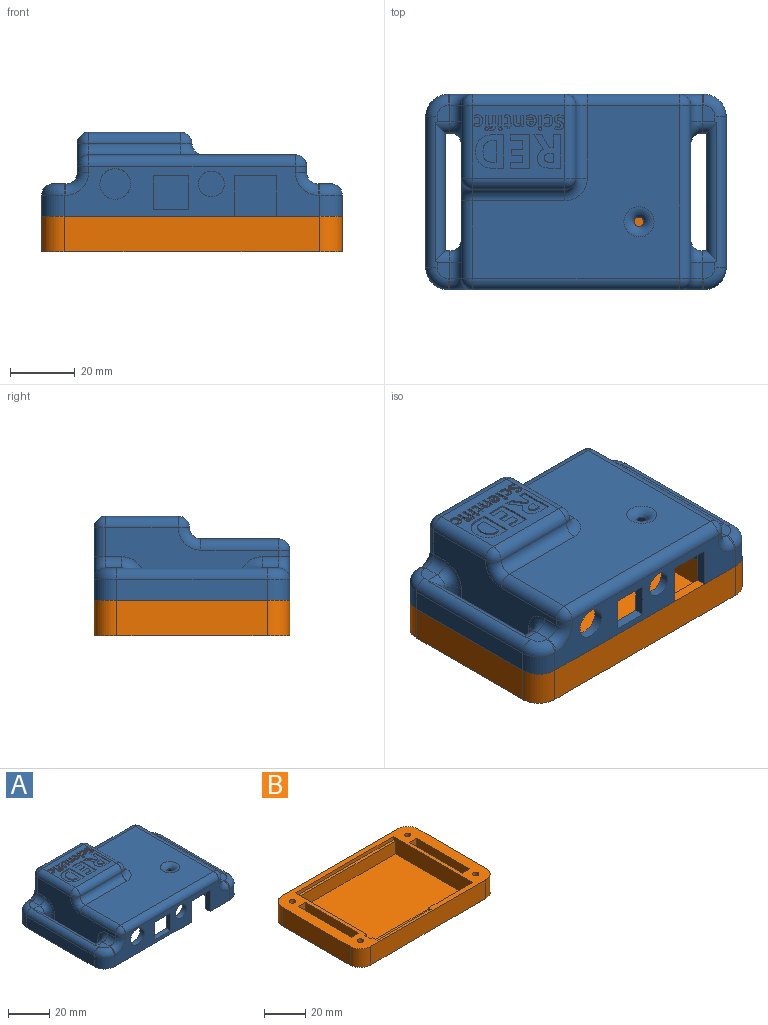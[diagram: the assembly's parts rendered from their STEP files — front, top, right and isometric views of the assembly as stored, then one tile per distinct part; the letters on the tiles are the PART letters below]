
ASSEMBLY  parts=2 mates=1
PART A: 327 faces, bbox 94.2x61.7x26 mm
  f0: plane 28.5x22.5mm, normal (0,0,1), area 406.2mm2, adj f59,f61,f65,f67,f109,f110,f111,f112
  f1: plane 5x4mm, normal (0,0,1), area 17.4mm2, adj f56,f57,f62,f69,f70
  f2: plane 5x4mm, normal (0,0,1), area 17.4mm2, adj f74,f76,f82,f83,f90
  f3: plane 79x15.5mm, normal (0,-1,0), area 711.4mm2, adj f5,f11,f19,f29,f30,f31,f32,f33
  f4: plane 67x17mm, normal (0,1,0), area 739.9mm2, adj f5,f25,f26,f27,f29,f30,f31,f32
  f5: plane 93x60.5mm, normal (0,0,-1), area 1410.7mm2, adj f3,f4,f6,f7,f8,f10,f11,f12
  f6: plane 53.5x22.5mm, normal (-1,0,0), area 694.3mm2, adj f5,f46,f47,f50,f51,f58,f59,f63
  f7: plane 53.5x15.5mm, normal (1,0,0), area 526.3mm2, adj f5,f73,f74,f75,f87,f88,f93,f96
  f8: plane 79x22.5mm, normal (0,1,0), area 1320.5mm2, adj f5,f13,f17,f48,f49,f51,f61,f76
  f9: plane 64x53.5mm, normal (0,0,1), area 2319mm2, adj f66,f71,f72,f85,f86,f95,f96,f108
  f10: plane 6.5x1.5mm, normal (0,1,0), area 9.8mm2, adj f5,f15,f88,f89
  f11: cylinder r=7mm len=7mm, axis (0,0,-1), area 71.5mm2, adj f3,f5,f12,f94
  f12: plane 46.5x6.5mm, normal (1,0,0), area 302.2mm2, adj f5,f11,f13,f90
  f13: cylinder r=7mm len=7mm, axis (0,0,-1), area 71.5mm2, adj f5,f8,f12,f83
  f14: plane 6.5x1.5mm, normal (0,-1,0), area 9.8mm2, adj f5,f15,f73,f82
  f15: plane 36.5x6.5mm, normal (-1,0,0), area 237.2mm2, adj f5,f10,f14,f81
  f16: plane 5x4mm, normal (0,0,1), area 17.4mm2, adj f89,f90,f94,f97,f98
  f17: cylinder r=7mm len=7mm, axis (0,0,-1), area 71.5mm2, adj f5,f8,f18,f52
  f18: plane 46.5x6.5mm, normal (-1,0,0), area 302.2mm2, adj f5,f17,f19,f56
  f19: cylinder r=7mm len=7mm, axis (0,0,-1), area 71.5mm2, adj f3,f5,f18,f62
  f20: plane 6.5x1.5mm, normal (0,1,0), area 9.8mm2, adj f5,f21,f57,f58
  f21: plane 36.5x6.5mm, normal (1,0,0), area 237.3mm2, adj f5,f20,f22,f54
  f22: plane 6.5x1.5mm, normal (0,-1,0), area 9.8mm2, adj f5,f21,f47,f53
  f23: plane 5x4mm, normal (0,0,1), area 17.4mm2, adj f46,f49,f52,f53,f56
  f24: plane 67x20.5mm, normal (0,-1,0), area 1251.9mm2, adj f5,f25,f26,f27,f102,f106
  f25: plane 56x20.5mm, normal (1,0,0), area 1045.6mm2, adj f4,f5,f24,f27,f103,f107
  f26: plane 56x17mm, normal (-1,0,0), area 952mm2, adj f4,f5,f24,f27
  f27: plane 67x56mm, normal (0,0,-1), area 2712.4mm2, adj f4,f24,f25,f26,f102,f103,f108
  f28: plane 24.5x19mm, normal (0,0,-1), area 465.5mm2, adj f104,f105,f106,f107
  f29: plane 11x3mm, normal (0,0,-1), area 33mm2, adj f3,f4,f30,f32
  f30: plane 10.5x3mm, normal (1,0,0), area 31.5mm2, adj f3,f4,f29,f31
  f31: plane 11x3mm, normal (0,0,1), area 33mm2, adj f3,f4,f30,f32
  f32: plane 10.5x3mm, normal (-1,0,0), area 31.5mm2, adj f3,f4,f29,f31
  f33: plane 12.5x3mm, normal (-1,0,0), area 37.5mm2, adj f3,f4,f5,f34
  f34: plane 13x3mm, normal (0,0,-1), area 39mm2, adj f3,f4,f33,f35
  f35: plane 12.5x3mm, normal (1,0,0), area 37.5mm2, adj f3,f4,f5,f34
  f36: cylinder r=4mm len=8mm, axis (0,-1,0), area 75.4mm2, adj f3,f4
  f37: cylinder r=4.75mm len=9.5mm, axis (0,-1,0), area 89.5mm2, adj f3,f4
  f38: cone r=0mm half-angle=59deg, axis (0,0,-1), area 8.2mm2, adj f39
  f39: cylinder r=1.5mm len=5mm, axis (0,0,-1), area 47.1mm2, adj f5,f38
  f40: cone r=0mm half-angle=59deg, axis (0,0,-1), area 8.2mm2, adj f41
  f41: cylinder r=1.5mm len=5mm, axis (0,0,-1), area 47.1mm2, adj f5,f40
  f42: cone r=0mm half-angle=59deg, axis (0,0,-1), area 8.2mm2, adj f43
  f43: cylinder r=1.5mm len=5mm, axis (0,0,-1), area 47.1mm2, adj f5,f42
  f44: cone r=0mm half-angle=59deg, axis (0,0,-1), area 8.2mm2, adj f45
  f45: cylinder r=1.5mm len=5mm, axis (0,0,-1), area 47.1mm2, adj f5,f44
  f46: cylinder r=3.5mm len=5mm, axis (0,1,0), area 27.5mm2, adj f6,f23,f48,f50
  f47: cylinder r=3.5mm len=6.5mm, axis (0,0,-1), area 35.7mm2, adj f5,f6,f22,f50
  f48: torus R=7mm, axis (0,1,0), area 41.2mm2, adj f8,f46,f49,f51
  f49: cylinder r=3.5mm len=3.5mm, axis (-1,0,0), area 2.7mm2, adj f8,f23,f48,f52
  f50: torus R=7mm, axis (1,0,0), area 41.2mm2, adj f6,f46,f47,f53
  f51: cylinder r=3.5mm len=9mm, axis (0,0,1), area 49.5mm2, adj f6,f8,f48,f55
  f52: torus R=3.5mm, axis (0,0,1), area 49.5mm2, adj f17,f23,f49,f56
  f53: cylinder r=3.5mm len=4.5mm, axis (-1,0,0), area 15mm2, adj f22,f23,f50,f54,f56
  f54: cylinder r=3.5mm len=42.5mm, axis (0,-1,0), area 193.1mm2, adj f21,f53,f56,f57
  f55: sphere r=3.5mm, area 19.2mm2, adj f51,f59,f61
  f56: cylinder r=3.5mm len=46.5mm, axis (0,1,0), area 234.1mm2, adj f1,f18,f23,f52,f53,f54,f57,f62
  f57: cylinder r=3.5mm len=4.5mm, axis (1,0,0), area 15mm2, adj f1,f20,f54,f56,f63
  f58: cylinder r=3.5mm len=6.5mm, axis (0,0,1), area 35.7mm2, adj f5,f6,f20,f63
  f59: cylinder r=3.5mm len=22.5mm, axis (0,-1,0), area 123.7mm2, adj f0,f6,f55,f64
  f60: sphere r=3.5mm, area 19.2mm2, adj f65,f66,f67
  f61: cylinder r=3.5mm len=28.5mm, axis (1,0,0), area 156.7mm2, adj f0,f8,f55,f68
  f62: torus R=3.5mm, axis (0,0,1), area 49.5mm2, adj f1,f19,f56,f69
  f63: torus R=7mm, axis (1,0,0), area 41.2mm2, adj f6,f57,f58,f70
  f64: sphere r=3.5mm, area 19.2mm2, adj f59,f65,f78
  f65: cylinder r=3.5mm len=28.5mm, axis (-1,0,0), area 156.7mm2, adj f0,f60,f64,f71
  f66: torus R=7mm, axis (0,0,1), area 41.2mm2, adj f9,f60,f71,f72
  f67: cylinder r=3.5mm len=22.5mm, axis (0,-1,0), area 123.7mm2, adj f0,f60,f68,f72
  f68: sphere r=3.5mm, area 19.2mm2, adj f61,f67,f79
  f69: cylinder r=3.5mm len=3.5mm, axis (-1,0,0), area 2.7mm2, adj f1,f3,f62,f77
  f70: cylinder r=3.5mm len=5mm, axis (0,-1,0), area 27.5mm2, adj f1,f6,f63,f77
  f71: cylinder r=3.5mm len=28.5mm, axis (1,0,0), area 156.7mm2, adj f9,f65,f66,f78
  f72: cylinder r=3.5mm len=22.5mm, axis (0,1,0), area 123.7mm2, adj f9,f66,f67,f79
  f73: cylinder r=3.5mm len=6.5mm, axis (0,0,-1), area 35.7mm2, adj f5,f7,f14,f75
  f74: cylinder r=3.5mm len=5mm, axis (0,-1,0), area 27.5mm2, adj f2,f7,f75,f80
  f75: torus R=7mm, axis (1,0,0), area 41.2mm2, adj f7,f73,f74,f82
  f76: cylinder r=3.5mm len=3.5mm, axis (1,0,0), area 2.7mm2, adj f2,f8,f80,f83
  f77: torus R=7mm, axis (0,1,0), area 41.2mm2, adj f3,f69,f70,f84
  f78: torus R=7mm, axis (1,0,0), area 41.2mm2, adj f6,f64,f71,f85
  f79: torus R=7mm, axis (0,1,0), area 41.2mm2, adj f8,f68,f72,f86
  f80: torus R=7mm, axis (0,1,0), area 41.2mm2, adj f8,f74,f76,f87
  f81: cylinder r=3.5mm len=42.5mm, axis (0,1,0), area 193.1mm2, adj f15,f82,f89,f90
  f82: cylinder r=3.5mm len=4.5mm, axis (-1,0,0), area 15mm2, adj f2,f14,f75,f81,f90
  f83: torus R=3.5mm, axis (0,0,1), area 49.5mm2, adj f2,f13,f76,f90
  f84: cylinder r=3.5mm len=3.5mm, axis (0,0,-1), area 11mm2, adj f3,f6,f77,f91
  f85: cylinder r=3.5mm len=24mm, axis (0,1,0), area 131.9mm2, adj f6,f9,f78,f91
  f86: cylinder r=3.5mm len=28.5mm, axis (1,0,0), area 156.7mm2, adj f8,f9,f79,f92
  f87: cylinder r=3.5mm len=3.5mm, axis (0,0,-1), area 11mm2, adj f7,f8,f80,f92
  f88: cylinder r=3.5mm len=6.5mm, axis (0,0,1), area 35.7mm2, adj f5,f7,f10,f93
  f89: cylinder r=3.5mm len=4.5mm, axis (1,0,0), area 15mm2, adj f10,f16,f81,f90,f93
  f90: cylinder r=3.5mm len=46.5mm, axis (0,-1,0), area 234.1mm2, adj f2,f12,f16,f81,f82,f83,f89,f94
  f91: sphere r=3.5mm, area 19.2mm2, adj f84,f85,f95
  f92: sphere r=3.5mm, area 19.2mm2, adj f86,f87,f96
  f93: torus R=7mm, axis (1,0,0), area 41.2mm2, adj f7,f88,f89,f97
  f94: torus R=3.5mm, axis (0,0,1), area 49.5mm2, adj f11,f16,f90,f98
  f95: cylinder r=3.5mm len=64mm, axis (-1,0,0), area 351.9mm2, adj f3,f9,f91,f99
  f96: cylinder r=3.5mm len=53.5mm, axis (0,-1,0), area 294.1mm2, adj f7,f9,f92,f99
  f97: cylinder r=3.5mm len=5mm, axis (0,1,0), area 27.5mm2, adj f7,f16,f93,f100
  f98: cylinder r=3.5mm len=3.5mm, axis (1,0,0), area 2.7mm2, adj f3,f16,f94,f100
  f99: sphere r=3.5mm, area 19.2mm2, adj f95,f96,f101
  f100: torus R=7mm, axis (0,1,0), area 41.2mm2, adj f3,f97,f98,f101
  f101: cylinder r=3.5mm len=3.5mm, axis (0,0,1), area 11mm2, adj f3,f7,f99,f100
  f102: cylinder r=3.5mm len=29.5mm, axis (0,-1,0), area 149.9mm2, adj f24,f27,f103,f104
  f103: cylinder r=3.5mm len=35mm, axis (-1,0,0), area 180.2mm2, adj f25,f27,f102,f105
  f104: cylinder r=3.5mm len=26mm, axis (0,1,0), area 129mm2, adj f28,f102,f105,f106
  f105: cylinder r=3.5mm len=31.5mm, axis (1,0,0), area 159.2mm2, adj f28,f103,f104,f107
  f106: cylinder r=3.5mm len=31.5mm, axis (-1,0,0), area 159.2mm2, adj f24,f28,f104,f107
  f107: cylinder r=3.5mm len=26mm, axis (0,-1,0), area 129mm2, adj f25,f28,f105,f106
  f108: torus R=4.66mm, axis (0,0,1), area 71.7mm2, adj f9,f27
  f109: plane 3.97x0.5mm, normal (1,0,0), area 2mm2, adj f0,f110,f127,f128
  f110: plane 1.17x0.5mm, normal (0,-1,0), area 0.6mm2, adj f0,f109,f111,f128
  f111: plane 3.97x2.47mm, normal (-0.85,-0.53,0), area 2.3mm2, adj f0,f110,f112,f128
  f112: plane 2.43x0.5mm, normal (0,-1,0), area 1.2mm2, adj f0,f111,f113,f128
  f113: extruded ~4.51x3.04mm, area 2.7mm2, adj f0,f112,f114,f128
  f114: extruded ~1.42x1.11mm, area 0.9mm2, adj f0,f113,f115,f128
  f115: extruded ~1.62x0.5mm, area 0.9mm2, adj f0,f114,f116,f128
  f116: extruded ~2.33x1.01mm, area 1.3mm2, adj f0,f115,f117,f128
  f117: extruded ~3.12x0.77mm, area 1.6mm2, adj f0,f116,f118,f128
  f118: plane 3.01x0.5mm, normal (0,1,0), area 1.5mm2, adj f0,f117,f119,f128
  f119: plane 10.34x0.5mm, normal (-1,0,0), area 5.2mm2, adj f0,f118,f127,f128
  f120: plane 0.71x0.5mm, normal (0,1,0), area 0.4mm2, adj f121,f126,f128,f129
  f121: plane 2.79x0.5mm, normal (1,0,0), area 1.4mm2, adj f120,f122,f128,f129
  f122: plane 0.67x0.5mm, normal (0,-1,0), area 0.3mm2, adj f121,f123,f128,f129
  f123: extruded ~1.57x0.5mm, area 0.8mm2, adj f122,f124,f128,f129
  f124: extruded ~1.05x0.51mm, area 0.6mm2, adj f123,f125,f128,f129
  f125: extruded ~1.09x0.5mm, area 0.6mm2, adj f124,f126,f128,f129
  f126: extruded ~1.54x0.5mm, area 0.8mm2, adj f120,f125,f128,f129
  f127: plane 2.19x0.5mm, normal (0,-1,0), area 1.1mm2, adj f0,f109,f119,f128
  f128: plane 10.34x8.26mm, normal (0,0,1), area 52.2mm2, adj f109,f110,f111,f112,f113,f114,f115,f116
  f129: plane 2.79x2.74mm, normal (0,0,1), area 6.7mm2, adj f120,f121,f122,f123,f124,f125,f126
  f130: extruded ~1.73x1.58mm, area 1.3mm2, adj f0,f131,f143,f144
  f131: extruded ~0.58x0.5mm, area 0.3mm2, adj f0,f130,f132,f144
  f132: extruded ~0.5x0.45mm, area 0.2mm2, adj f0,f131,f133,f144
  f133: plane 0.79x0.5mm, normal (1,0,0), area 0.4mm2, adj f0,f132,f134,f144
  f134: extruded ~0.5x0.45mm, area 0.3mm2, adj f0,f133,f135,f144
  f135: extruded ~0.5x0.49mm, area 0.3mm2, adj f0,f134,f136,f144
  f136: extruded ~0.99x0.72mm, area 0.7mm2, adj f0,f135,f137,f144
  f137: extruded ~1.02x0.72mm, area 0.7mm2, adj f0,f136,f138,f144
  f138: extruded ~0.5x0.38mm, area 0.2mm2, adj f0,f137,f139,f144
  f139: extruded ~0.5x0.41mm, area 0.2mm2, adj f0,f138,f140,f144
  f140: plane 0.72x0.5mm, normal (0.93,-0.36,0), area 0.4mm2, adj f0,f139,f141,f144
  f141: extruded ~1.05x0.5mm, area 0.5mm2, adj f0,f140,f142,f144
  f142: extruded ~1.23x0.5mm, area 0.7mm2, adj f0,f141,f143,f144
  f143: extruded ~1.32x0.5mm, area 0.7mm2, adj f0,f130,f142,f144
  f144: plane 3.51x2.72mm, normal (0,0,1), area 5.1mm2, adj f130,f131,f132,f133,f134,f135,f136,f137
  f145: extruded ~0.5x0.5mm, area 0.4mm2, adj f0,f146,f149,f150
  f146: extruded ~0.5x0.5mm, area 0.4mm2, adj f0,f145,f147,f150
  f147: extruded ~0.5x0.38mm, area 0.2mm2, adj f0,f146,f148,f150
  f148: extruded ~0.5x0.33mm, area 0.2mm2, adj f0,f147,f149,f150
  f149: extruded ~0.5x0.5mm, area 0.4mm2, adj f0,f145,f148,f150
  f150: plane 1.01x0.91mm, normal (0,0,1), area 0.8mm2, adj f145,f146,f147,f148,f149
  f151: plane 0.92x0.5mm, normal (0,-1,0), area 0.5mm2, adj f0,f152,f154,f155
  f152: plane 3.38x0.5mm, normal (1,0,0), area 1.7mm2, adj f0,f151,f153,f155
  f153: plane 0.92x0.5mm, normal (0,1,0), area 0.5mm2, adj f0,f152,f154,f155
  f154: plane 3.38x0.5mm, normal (-1,0,0), area 1.7mm2, adj f0,f151,f153,f155
  f155: plane 3.38x0.92mm, normal (0,0,1), area 3.1mm2, adj f151,f152,f153,f154
  f156: extruded ~0.58x0.5mm, area 0.3mm2, adj f0,f157,f173,f174
  f157: extruded ~0.5x0.29mm, area 0.2mm2, adj f0,f156,f158,f174
  f158: extruded ~0.5x0.29mm, area 0.2mm2, adj f0,f157,f159,f174
  f159: plane 1.63x0.5mm, normal (1,0,0), area 0.8mm2, adj f0,f158,f160,f174
  f160: plane 0.95x0.5mm, normal (0,-1,0), area 0.5mm2, adj f0,f159,f161,f174
  f161: plane 0.69x0.5mm, normal (1,0,0), area 0.3mm2, adj f0,f160,f162,f174
  f162: plane 0.95x0.5mm, normal (0,1,0), area 0.5mm2, adj f0,f161,f163,f174
  f163: plane 0.72x0.5mm, normal (1,0,0), area 0.4mm2, adj f0,f162,f164,f174
  f164: plane 0.59x0.5mm, normal (0,1,0), area 0.3mm2, adj f0,f163,f165,f174
  f165: plane 0.72x0.5mm, normal (-0.94,0.35,0), area 0.4mm2, adj f0,f164,f166,f174
  f166: plane 0.51x0.5mm, normal (-0.52,0.85,0), area 0.3mm2, adj f0,f165,f167,f174
  f167: plane 0.5x0.39mm, normal (-1,0,0), area 0.2mm2, adj f0,f166,f168,f174
  f168: plane 0.5x0.44mm, normal (0,-1,0), area 0.2mm2, adj f0,f167,f169,f174
  f169: plane 1.63x0.5mm, normal (-1,0,0), area 0.8mm2, adj f0,f168,f170,f174
  f170: extruded ~0.84x0.5mm, area 0.4mm2, adj f0,f169,f171,f174
  f171: extruded ~0.81x0.5mm, area 0.4mm2, adj f0,f170,f172,f174
  f172: extruded ~0.85x0.5mm, area 0.4mm2, adj f0,f171,f173,f174
  f173: plane 0.69x0.5mm, normal (1,0,0), area 0.3mm2, adj f0,f156,f172,f174
  f174: plane 4.17x2.35mm, normal (0,0,1), area 5.1mm2, adj f156,f157,f158,f159,f160,f161,f162,f163
  f175: plane 0.92x0.5mm, normal (0,-1,0), area 0.5mm2, adj f0,f176,f178,f179
  f176: plane 3.38x0.5mm, normal (1,0,0), area 1.7mm2, adj f0,f175,f177,f179
  f177: plane 0.92x0.5mm, normal (0,1,0), area 0.5mm2, adj f0,f176,f178,f179
  f178: plane 3.38x0.5mm, normal (-1,0,0), area 1.7mm2, adj f0,f175,f177,f179
  f179: plane 3.38x0.92mm, normal (0,0,1), area 3.1mm2, adj f175,f176,f177,f178
  f180: extruded ~0.5x0.5mm, area 0.4mm2, adj f0,f181,f184,f185
  f181: extruded ~0.5x0.5mm, area 0.4mm2, adj f0,f180,f182,f185
  f182: extruded ~0.5x0.38mm, area 0.2mm2, adj f0,f181,f183,f185
  f183: extruded ~0.5x0.33mm, area 0.2mm2, adj f0,f182,f184,f185
  f184: extruded ~0.5x0.5mm, area 0.4mm2, adj f0,f180,f183,f185
  f185: plane 1.01x0.91mm, normal (0,0,1), area 0.8mm2, adj f180,f181,f182,f183,f184
  f186: plane 0.8x0.5mm, normal (0,-1,0), area 0.4mm2, adj f0,f187,f203,f204
  f187: plane 0.69x0.5mm, normal (1,0,0), area 0.3mm2, adj f0,f186,f188,f204
  f188: plane 0.8x0.5mm, normal (0,1,0), area 0.4mm2, adj f0,f187,f189,f204
  f189: plane 0.5x0.21mm, normal (1,0,0), area 0.1mm2, adj f0,f188,f190,f204
  f190: extruded ~0.5x0.3mm, area 0.2mm2, adj f0,f189,f191,f204
  f191: extruded ~0.5x0.28mm, area 0.2mm2, adj f0,f190,f192,f204
  f192: extruded ~0.51x0.5mm, area 0.3mm2, adj f0,f191,f193,f204
  f193: plane 0.68x0.5mm, normal (0.94,-0.33,0), area 0.4mm2, adj f0,f192,f194,f204
  f194: extruded ~0.85x0.5mm, area 0.4mm2, adj f0,f193,f195,f204
  f195: extruded ~0.91x0.5mm, area 0.5mm2, adj f0,f194,f196,f204
  f196: extruded ~0.84x0.5mm, area 0.5mm2, adj f0,f195,f197,f204
  f197: plane 0.5x0.25mm, normal (-1,0,0), area 0.1mm2, adj f0,f196,f198,f204
  f198: plane 0.51x0.5mm, normal (-0.44,0.9,0), area 0.3mm2, adj f0,f197,f199,f204
  f199: plane 0.5x0.45mm, normal (-1,0,0), area 0.2mm2, adj f0,f198,f200,f204
  f200: plane 0.51x0.5mm, normal (0,-1,0), area 0.3mm2, adj f0,f199,f201,f204
  f201: plane 2.69x0.5mm, normal (-1,0,0), area 1.3mm2, adj f0,f200,f202,f204
  f202: plane 0.92x0.5mm, normal (0,-1,0), area 0.5mm2, adj f0,f201,f203,f204
  f203: plane 2.69x0.5mm, normal (1,0,0), area 1.3mm2, adj f0,f186,f202,f204
  f204: plane 4.74x2.56mm, normal (0,0,1), area 5.8mm2, adj f186,f187,f188,f189,f190,f191,f192,f193
  f205: plane 5.96x0.5mm, normal (0,-1,0), area 3mm2, adj f0,f206,f216,f217
  f206: plane 1.81x0.5mm, normal (1,0,0), area 0.9mm2, adj f0,f205,f207,f217
  f207: plane 3.76x0.5mm, normal (0,1,0), area 1.9mm2, adj f0,f206,f208,f217
  f208: plane 2.67x0.5mm, normal (1,0,0), area 1.3mm2, adj f0,f207,f209,f217
  f209: plane 3.5x0.5mm, normal (0,-1,0), area 1.8mm2, adj f0,f208,f210,f217
  f210: plane 1.8x0.5mm, normal (1,0,0), area 0.9mm2, adj f0,f209,f211,f217
  f211: plane 3.5x0.5mm, normal (0,1,0), area 1.8mm2, adj f0,f210,f212,f217
  f212: plane 2.27x0.5mm, normal (1,0,0), area 1.1mm2, adj f0,f211,f213,f217
  f213: plane 3.76x0.5mm, normal (0,-1,0), area 1.9mm2, adj f0,f212,f214,f217
  f214: plane 1.8x0.5mm, normal (1,0,0), area 0.9mm2, adj f0,f213,f215,f217
  f215: plane 5.96x0.5mm, normal (0,1,0), area 3mm2, adj f0,f214,f216,f217
  f216: plane 10.34x0.5mm, normal (-1,0,0), area 5.2mm2, adj f0,f205,f215,f217
  f217: plane 10.34x5.96mm, normal (0,0,1), area 42.6mm2, adj f205,f206,f207,f208,f209,f210,f211,f212
  f218: extruded ~3.33x2.94mm, area 2.5mm2, adj f219,f229,f230,f326
  f219: extruded ~3.4x3.17mm, area 2.7mm2, adj f218,f220,f230,f326
  f220: plane 0.94x0.5mm, normal (0,1,0), area 0.5mm2, adj f219,f221,f230,f326
  f221: plane 6.73x0.5mm, normal (1,0,0), area 3.4mm2, adj f220,f229,f230,f326
  f222: extruded ~3.91x1.45mm, area 2.1mm2, adj f0,f223,f228,f230
  f223: extruded ~3.74x1.4mm, area 2.1mm2, adj f0,f222,f224,f230
  f224: extruded ~3.93x1.34mm, area 2.1mm2, adj f0,f223,f225,f230
  f225: plane 3.25x0.5mm, normal (0,1,0), area 1.6mm2, adj f0,f224,f226,f230
  f226: plane 10.34x0.5mm, normal (-1,0,0), area 5.2mm2, adj f0,f225,f227,f230
  f227: plane 2.93x0.5mm, normal (0,-1,0), area 1.5mm2, adj f0,f226,f228,f230
  f228: extruded ~4.2x1.36mm, area 2.3mm2, adj f0,f222,f227,f230
  f229: plane 1.17x0.5mm, normal (0,-1,0), area 0.6mm2, adj f218,f221,f230,f326
  f230: plane 10.34x8.58mm, normal (0,0,1), area 54.5mm2, adj f218,f219,f220,f221,f222,f223,f224,f225
  f231: extruded ~0.95x0.5mm, area 0.5mm2, adj f0,f232,f258,f259
  f232: extruded ~0.73x0.5mm, area 0.4mm2, adj f0,f231,f233,f259
  f233: extruded ~0.85x0.6mm, area 0.5mm2, adj f0,f232,f234,f259
  f234: extruded ~0.59x0.5mm, area 0.3mm2, adj f0,f233,f235,f259
  f235: extruded ~0.5x0.18mm, area 0.1mm2, adj f0,f234,f236,f259
  f236: extruded ~0.5x0.22mm, area 0.1mm2, adj f0,f235,f237,f259
  f237: extruded ~0.5x0.32mm, area 0.2mm2, adj f0,f236,f238,f259
  f238: extruded ~0.5x0.41mm, area 0.2mm2, adj f0,f237,f239,f259
  f239: extruded ~0.5x0.46mm, area 0.2mm2, adj f0,f238,f240,f259
  f240: extruded ~0.59x0.5mm, area 0.3mm2, adj f0,f239,f241,f259
  f241: plane 0.73x0.5mm, normal (0.92,-0.38,0), area 0.4mm2, adj f0,f240,f242,f259
  f242: extruded ~0.66x0.5mm, area 0.3mm2, adj f0,f241,f243,f259
  f243: extruded ~0.66x0.5mm, area 0.3mm2, adj f0,f242,f244,f259
  f244: extruded ~1.1x0.5mm, area 0.6mm2, adj f0,f243,f245,f259
  f245: extruded ~0.92x0.5mm, area 0.5mm2, adj f0,f244,f246,f259
  f246: extruded ~0.54x0.5mm, area 0.3mm2, adj f0,f245,f247,f259
  f247: extruded ~0.5x0.41mm, area 0.3mm2, adj f0,f246,f248,f259
  f248: extruded ~0.61x0.5mm, area 0.4mm2, adj f0,f247,f249,f259
  f249: extruded ~0.57x0.5mm, area 0.3mm2, adj f0,f248,f250,f259
  f250: extruded ~0.5x0.21mm, area 0.1mm2, adj f0,f249,f251,f259
  f251: extruded ~0.5x0.23mm, area 0.1mm2, adj f0,f250,f252,f259
  f252: extruded ~0.5x0.35mm, area 0.2mm2, adj f0,f251,f253,f259
  f253: extruded ~0.5x0.47mm, area 0.2mm2, adj f0,f252,f254,f259
  f254: extruded ~0.57x0.5mm, area 0.3mm2, adj f0,f253,f255,f259
  f255: extruded ~0.76x0.5mm, area 0.4mm2, adj f0,f254,f256,f259
  f256: plane 0.87x0.5mm, normal (-1,0,0), area 0.4mm2, adj f0,f255,f257,f259
  f257: extruded ~1.25x0.5mm, area 0.6mm2, adj f0,f256,f258,f259
  f258: extruded ~1.2x0.5mm, area 0.6mm2, adj f0,f231,f257,f259
  f259: plane 4.55x2.88mm, normal (0,0,1), area 7.4mm2, adj f231,f232,f233,f234,f235,f236,f237,f238
  f260: extruded ~1.73x1.58mm, area 1.3mm2, adj f0,f261,f273,f274
  f261: extruded ~0.58x0.5mm, area 0.3mm2, adj f0,f260,f262,f274
  f262: extruded ~0.5x0.45mm, area 0.2mm2, adj f0,f261,f263,f274
  f263: plane 0.79x0.5mm, normal (1,0,0), area 0.4mm2, adj f0,f262,f264,f274
  f264: extruded ~0.5x0.45mm, area 0.3mm2, adj f0,f263,f265,f274
  f265: extruded ~0.5x0.49mm, area 0.3mm2, adj f0,f264,f266,f274
  f266: extruded ~0.99x0.72mm, area 0.7mm2, adj f0,f265,f267,f274
  f267: extruded ~1.02x0.72mm, area 0.7mm2, adj f0,f266,f268,f274
  f268: extruded ~0.5x0.38mm, area 0.2mm2, adj f0,f267,f269,f274
  f269: extruded ~0.5x0.41mm, area 0.2mm2, adj f0,f268,f270,f274
  f270: plane 0.72x0.5mm, normal (0.93,-0.36,0), area 0.4mm2, adj f0,f269,f271,f274
  f271: extruded ~1.05x0.5mm, area 0.5mm2, adj f0,f270,f272,f274
  f272: extruded ~1.23x0.5mm, area 0.7mm2, adj f0,f271,f273,f274
  f273: extruded ~1.32x0.5mm, area 0.7mm2, adj f0,f260,f272,f274
  f274: plane 3.51x2.72mm, normal (0,0,1), area 5.1mm2, adj f260,f261,f262,f263,f264,f265,f266,f267
  f275: plane 0.92x0.5mm, normal (0,-1,0), area 0.5mm2, adj f0,f276,f278,f279
  f276: plane 3.38x0.5mm, normal (1,0,0), area 1.7mm2, adj f0,f275,f277,f279
  f277: plane 0.92x0.5mm, normal (0,1,0), area 0.5mm2, adj f0,f276,f278,f279
  f278: plane 3.38x0.5mm, normal (-1,0,0), area 1.7mm2, adj f0,f275,f277,f279
  f279: plane 3.38x0.92mm, normal (0,0,1), area 3.1mm2, adj f275,f276,f277,f278
  f280: extruded ~0.5x0.5mm, area 0.4mm2, adj f0,f281,f284,f285
  f281: extruded ~0.5x0.5mm, area 0.4mm2, adj f0,f280,f282,f285
  f282: extruded ~0.5x0.38mm, area 0.2mm2, adj f0,f281,f283,f285
  f283: extruded ~0.5x0.33mm, area 0.2mm2, adj f0,f282,f284,f285
  f284: extruded ~0.5x0.5mm, area 0.4mm2, adj f0,f280,f283,f285
  f285: plane 1.01x0.91mm, normal (0,0,1), area 0.8mm2, adj f280,f281,f282,f283,f284
  f286: extruded ~1.28x0.5mm, area 0.7mm2, adj f0,f287,f305,f306
  f287: extruded ~0.67x0.5mm, area 0.3mm2, adj f0,f286,f288,f306
  f288: extruded ~0.52x0.5mm, area 0.3mm2, adj f0,f287,f289,f306
  f289: plane 0.72x0.5mm, normal (1,0,0), area 0.4mm2, adj f0,f288,f290,f306
  f290: extruded ~0.57x0.5mm, area 0.3mm2, adj f0,f289,f291,f306
  f291: extruded ~0.58x0.5mm, area 0.3mm2, adj f0,f290,f292,f306
  f292: extruded ~0.61x0.5mm, area 0.3mm2, adj f0,f291,f293,f306
  f293: extruded ~0.61x0.5mm, area 0.3mm2, adj f0,f292,f294,f306
  f294: plane 2.18x0.5mm, normal (0,-1,0), area 1.1mm2, adj f0,f293,f295,f306
  f295: plane 0.5x0.45mm, normal (1,0,0), area 0.2mm2, adj f0,f294,f296,f306
  f296: extruded ~1.13x0.5mm, area 0.6mm2, adj f0,f295,f297,f306
  f297: extruded ~1.12x0.5mm, area 0.6mm2, adj f0,f296,f298,f306
  f298: extruded ~1.18x0.5mm, area 0.7mm2, adj f0,f297,f299,f306
  f299: extruded ~1.32x0.5mm, area 0.7mm2, adj f0,f298,f305,f306
  f300: extruded ~0.5x0.46mm, area 0.3mm2, adj f301,f304,f306,f307
  f301: extruded ~0.5x0.47mm, area 0.3mm2, adj f300,f302,f306,f307
  f302: extruded ~0.53x0.5mm, area 0.3mm2, adj f301,f303,f306,f307
  f303: plane 1.3x0.5mm, normal (0,1,0), area 0.6mm2, adj f302,f304,f306,f307
  f304: extruded ~0.53x0.5mm, area 0.3mm2, adj f300,f303,f306,f307
  f305: extruded ~1.28x0.5mm, area 0.7mm2, adj f0,f286,f299,f306
  f306: plane 3.51x3.12mm, normal (0,0,1), area 6.9mm2, adj f286,f287,f288,f289,f290,f291,f292,f293
  f307: plane 1.3x0.71mm, normal (0,0,1), area 0.7mm2, adj f300,f301,f302,f303,f304
  f308: plane 0.92x0.5mm, normal (0,-1,0), area 0.5mm2, adj f0,f309,f324,f325
  f309: plane 2.21x0.5mm, normal (1,0,0), area 1.1mm2, adj f0,f308,f310,f325
  f310: extruded ~0.92x0.5mm, area 0.5mm2, adj f0,f309,f311,f325
  f311: extruded ~0.9x0.5mm, area 0.5mm2, adj f0,f310,f312,f325
  f312: extruded ~0.62x0.5mm, area 0.3mm2, adj f0,f311,f313,f325
  f313: extruded ~0.5x0.43mm, area 0.3mm2, adj f0,f312,f314,f325
  f314: plane 0.5x0.05mm, normal (0,1,0), area 0mm2, adj f0,f313,f315,f325
  f315: plane 0.5x0.43mm, normal (0.96,0.28,0), area 0.2mm2, adj f0,f314,f316,f325
  f316: plane 0.71x0.5mm, normal (0,1,0), area 0.4mm2, adj f0,f315,f317,f325
  f317: plane 3.38x0.5mm, normal (-1,0,0), area 1.7mm2, adj f0,f316,f318,f325
  f318: plane 0.92x0.5mm, normal (0,-1,0), area 0.5mm2, adj f0,f317,f319,f325
  f319: plane 1.59x0.5mm, normal (1,0,0), area 0.8mm2, adj f0,f318,f320,f325
  f320: extruded ~0.86x0.5mm, area 0.4mm2, adj f0,f319,f321,f325
  f321: extruded ~0.56x0.5mm, area 0.3mm2, adj f0,f320,f322,f325
  f322: extruded ~0.5x0.42mm, area 0.2mm2, adj f0,f321,f323,f325
  f323: extruded ~0.55x0.5mm, area 0.3mm2, adj f0,f322,f324,f325
  f324: plane 1.98x0.5mm, normal (-1,0,0), area 1mm2, adj f0,f308,f323,f325
  f325: plane 3.45x3.12mm, normal (0,0,1), area 7mm2, adj f308,f309,f310,f311,f312,f313,f314,f315
  f326: plane 6.73x4.11mm, normal (0,0,1), area 24.2mm2, adj f218,f219,f220,f221,f229
PART B: 63 faces, bbox 93x60.5x11 mm
  f0: plane 60.5x17.43mm, normal (0,0,-1), area 1054.2mm2, adj f5,f16,f58,f61
  f1: plane 60.5x17.63mm, normal (0,0,-1), area 1066.3mm2, adj f5,f16,f52,f57
  f2: plane 60.5x17.63mm, normal (0,0,-1), area 1066.3mm2, adj f5,f16,f48,f55
  f3: plane 60.5x17.43mm, normal (0,0,-1), area 1054.2mm2, adj f5,f16,f49,f51
  f4: plane 60.5x11.2mm, normal (0,0,-1), area 154.5mm2, adj f5,f13,f14,f15,f16,f20,f21,f27
  f5: plane 79x11mm, normal (0,1,0), area 868.9mm2, adj f0,f1,f2,f3,f4,f6,f19,f20
  f6: plane 60.5x11.2mm, normal (0,0,-1), area 154.5mm2, adj f5,f16,f17,f18,f19,f24,f25,f29
  f7: plane 8x4mm, normal (1,0,0), area 32mm2, adj f23,f31,f33,f37
  f8: plane 67x2mm, normal (0,-1,0), area 134mm2, adj f11,f12,f31,f36
  f9: plane 37x2mm, normal (0,1,0), area 74mm2, adj f10,f22,f31,f32
  f10: plane 3x2mm, normal (1,0,0), area 6mm2, adj f9,f31,f32,f33
  f11: plane 49x9.5mm, normal (1,0,0), area 454.2mm2, adj f8,f23,f31,f34,f35,f36
  f12: plane 54.5x9.5mm, normal (-1,0,0), area 495.2mm2, adj f8,f28,f31,f32,f33,f34,f35,f36
  f13: plane 11x11mm, normal (0,-1,0), area 62.7mm2, adj f4,f14,f30,f31,f47
  f14: plane 36.5x11mm, normal (-1,0,0), area 401.5mm2, adj f4,f13,f15,f31
  f15: plane 11x11mm, normal (0,1,0), area 62.7mm2, adj f4,f14,f30,f31,f47
  f16: plane 79x11mm, normal (0,-1,0), area 868.9mm2, adj f0,f1,f2,f3,f4,f6,f17,f27
  f17: cylinder r=7mm len=11mm, axis (0,0,-1), area 121mm2, adj f6,f16,f18,f31
  f18: plane 46.5x11mm, normal (1,0,0), area 511.5mm2, adj f6,f17,f19,f31,f46
  f19: cylinder r=7mm len=11mm, axis (0,0,-1), area 121mm2, adj f5,f6,f18,f31
  f20: cylinder r=7mm len=11mm, axis (0,0,-1), area 121mm2, adj f4,f5,f21,f31
  f21: plane 46.5x11mm, normal (-1,0,0), area 511.5mm2, adj f4,f20,f27,f31,f47
  f22: plane 2x1.5mm, normal (-1,0,0), area 3mm2, adj f9,f28,f31,f32
  f23: plane 9.5x1.5mm, normal (0,-1,0), area 13.8mm2, adj f7,f11,f31,f37
  f24: plane 36.5x11mm, normal (1,0,0), area 401.5mm2, adj f6,f25,f29,f31
  f25: plane 11x11mm, normal (0,-1,0), area 62.7mm2, adj f6,f24,f26,f31,f46
  f26: plane 36.5x5mm, normal (-1,0,0), area 182.5mm2, adj f25,f29,f31,f46
  f27: cylinder r=7mm len=11mm, axis (0,0,-1), area 121mm2, adj f4,f16,f21,f31
  f28: plane 30x2mm, normal (0,1,0), area 60mm2, adj f12,f22,f31,f32
  f29: plane 11x11mm, normal (0,1,0), area 62.7mm2, adj f6,f24,f26,f31,f46
  f30: plane 36.5x5mm, normal (1,0,0), area 182.5mm2, adj f13,f15,f31,f47
  f31: plane 93x60.5mm, normal (0,0,1), area 1478.2mm2, adj f5,f7,f8,f9,f10,f11,f12,f13
  f32: plane 67x3mm, normal (0,0,1), area 156mm2, adj f9,f10,f12,f22,f28,f33
  f33: plane 68.5x9.5mm, normal (0,1,0), area 516.3mm2, adj f7,f10,f12,f31,f32,f35,f37
  f34: plane 67x7.5mm, normal (0,-1,0), area 502.5mm2, adj f11,f12,f35,f36
  f35: plane 67x51.5mm, normal (0,0,1), area 3450.5mm2, adj f11,f12,f33,f34,f37
  f36: plane 67x1.5mm, normal (0,0,1), area 100.5mm2, adj f8,f11,f12,f34
  f37: cylinder r=1.5mm len=4mm, axis (0,1,0), area 9.4mm2, adj f7,f23,f33,f35
  f38: cylinder r=1.5mm len=8.5mm, axis (0,0,-1), area 80.1mm2, adj f31,f39
  f39: cone r=1.5mm half-angle=45deg, axis (0,0,-1), area 61.1mm2, adj f4,f38
  f40: cylinder r=1.5mm len=8.5mm, axis (0,0,-1), area 80.1mm2, adj f31,f41
  f41: cone r=1.5mm half-angle=45deg, axis (0,0,-1), area 61.1mm2, adj f4,f40
  f42: cylinder r=1.5mm len=8.5mm, axis (0,0,-1), area 80.1mm2, adj f31,f43
  f43: cone r=1.5mm half-angle=45deg, axis (0,0,-1), area 61.1mm2, adj f6,f42
  f44: cylinder r=1.5mm len=8.5mm, axis (0,0,-1), area 80.1mm2, adj f31,f45
  f45: cone r=1.5mm half-angle=45deg, axis (0,0,-1), area 61.1mm2, adj f6,f44
  f46: cylinder r=6mm len=36.5mm, axis (0,-1,0), area 344mm2, adj f18,f25,f26,f29
  f47: cylinder r=6mm len=36.5mm, axis (0,1,0), area 344mm2, adj f13,f15,f21,f30
  f48: plane 60.5x0.1mm, normal (1,0,0), area 6mm2, adj f2,f5,f16,f50
  f49: plane 60.5x0.1mm, normal (-1,0,0), area 6mm2, adj f3,f5,f16,f50
  f50: plane 60.5x0.1mm, normal (0,0,-1), area 6.1mm2, adj f5,f16,f48,f49
  f51: plane 60.5x0.1mm, normal (1,0,0), area 6.1mm2, adj f3,f5,f16,f53
  f52: plane 60.5x0.1mm, normal (-1,0,0), area 6mm2, adj f1,f5,f16,f53
  f53: plane 60.5x0.1mm, normal (0,0,-1), area 6.1mm2, adj f5,f16,f51,f52
  f54: plane 60.5x0.1mm, normal (1,0,0), area 6.1mm2, adj f4,f5,f16,f56
  f55: plane 60.5x0.1mm, normal (-1,0,0), area 6.1mm2, adj f2,f5,f16,f56
  f56: plane 60.5x0.1mm, normal (0,0,-1), area 6.1mm2, adj f5,f16,f54,f55
  f57: plane 60.5x0.1mm, normal (1,0,0), area 6mm2, adj f1,f5,f16,f59
  f58: plane 60.5x0.1mm, normal (-1,0,0), area 6mm2, adj f0,f5,f16,f59
  f59: plane 60.5x0.1mm, normal (0,0,-1), area 6mm2, adj f5,f16,f57,f58
  f60: plane 60.5x0.1mm, normal (-1,0,0), area 6mm2, adj f5,f6,f16,f62
  f61: plane 60.5x0.1mm, normal (1,0,0), area 6mm2, adj f0,f5,f16,f62
  f62: plane 60.5x0.1mm, normal (0,0,-1), area 6.1mm2, adj f5,f16,f60,f61
PLACE A t=(-51.23,-39.58,-1.59)mm
PLACE B t=(-17.73,-40.33,-12.59)mm
MATE fastened B.f27 <-> A.f19  axis (0,0,1) through (-90.73,-63.58,-1.59)mm
